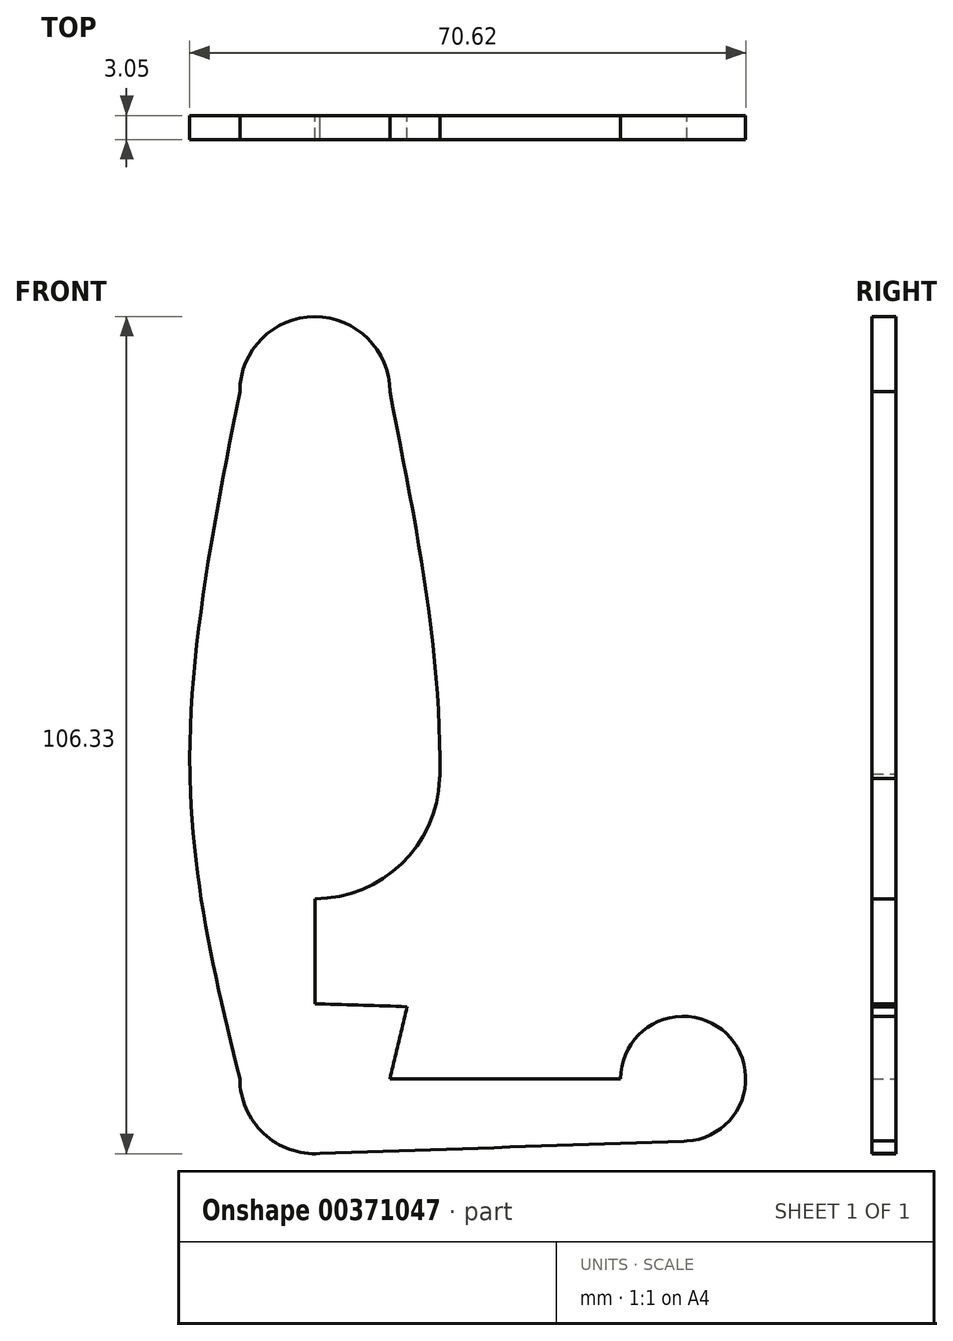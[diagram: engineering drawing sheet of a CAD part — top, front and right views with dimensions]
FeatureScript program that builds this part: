
annotation { "Feature Type Name" : "Feature", "Feature Type Description" : "" }
export const myFeature = defineFeature(function(context is Context, id is Id, definition is map)
    precondition{}
    {
        {
            var Q0;
            Q0=qCreatedBy(makeId("Front.planeOp"),FACE);
            var sketch = newSketch(context, id + "F0", { "sketchPlane" : qUnion([Q0])});
            skLineSegment(sketch, "E0", {"start": v(0, 0) * mm, "end": v(0, -38.73) * mm});
            skLineSegment(sketch, "E1", {"start": v(0, -38.73) * mm, "end": v(46.79, -38.73) * mm});
            skLineSegment(sketch, "E2", {"start": v(0, 0) * mm, "end": v(0, 48.56) * mm});
            skCircle(sketch, "E3", {"center": v(0, 48.56) * mm, "radius": 9.53 * mm});
            skCircle(sketch, "E4", {"center": v(0, 0) * mm, "radius": 15.88 * mm});
            skCircle(sketch, "E5", {"center": v(0, -38.73) * mm, "radius": 9.53 * mm});
            skCircle(sketch, "E6", {"center": v(46.79, -38.73) * mm, "radius": 7.94 * mm});
            skFitSpline(sketch, "E7", {"points": [v(-9.53, 48.56) * mm, v(-15.88, 0) * mm, v(-9.52, -38.73) * mm], "startDerivative": vector(-18.76, -94.67) * mm, "endDerivative": vector(19.46, -79.62) * mm});
            skFitSpline(sketch, "E8", {"points": [v(9.53, 48.56) * mm, v(15.88, 0) * mm, v(9.52, -38.73) * mm], "startDerivative": vector(18.76, -94.67) * mm, "endDerivative": vector(-19.46, -79.62) * mm});
            skFitSpline(sketch, "E9", {"points": [v(0, -29.2) * mm, v(46.68, -30.8) * mm, v(46.49, -30.8) * mm], "startDerivative": vector(74.56, -2.34) * mm, "endDerivative": vector(-4.82, -0.25) * mm});
            skFitSpline(sketch, "E10", {"points": [v(0, -48.25) * mm, v(47.24, -46.65) * mm], "startDerivative": vector(47.25, 1.59) * mm, "endDerivative": vector(47.25, 1.59) * mm});
            skSolve(sketch);
        }
        {
            var Q0;
            {var subQ0=sQuery(id+"F0.wireOp",EDGE,"E8");var subQ1=sQuery(id+"F0.wireOp",EDGE,"E4");var subQ2=makeQuery(id+"F0.imprint","INTERSECT",VERTEX,{"disambiguationData":[OD(1.0)],"derivedFrom":[subQ1,subQ0]});Q0=makeQuery(id+"F0.imprint","IMPRINT",FACE,{"disambiguationData":[TD([[makeQuery(id+"F0.imprint","IMPRINT",EDGE,{"disambiguationData":[TD([[subQ2,1.0]])],"derivedFrom":subQ1}),-1.0]])]});}
            var Q1;
            {var subQ1=sQuery(id+"F0.wireOp",EDGE,"E6");var subQ8=makeQuery(id+"F0.imprint","IMPRINT",VERTEX,{"derivedFrom":subQ1});Q1=makeQuery(id+"F0.imprint","IMPRINT",FACE,{"disambiguationData":[TD([[makeQuery(id+"F0.imprint","IMPRINT",EDGE,{"disambiguationData":[TD([[subQ8,1.0]])],"derivedFrom":subQ1}),1.0]])]});}
            var Q2;
            {var subQ3=sQuery(id+"F0.wireOp",EDGE,"E0");var subQ6=sQuery(id+"F0.wireOp",EDGE,"E2");var subQ8=makeQuery(id+"F0.imprint","INTERSECT",VERTEX,{"derivedFrom":[subQ3,subQ6]});Q2=makeQuery(id+"F0.imprint","IMPRINT",FACE,{"disambiguationData":[TD([[makeQuery(id+"F0.imprint","IMPRINT",EDGE,{"disambiguationData":[TD([[subQ8,-1.0]])],"derivedFrom":subQ3}),1.0]])]});}
            var Q3;
            {var subQ1=sQuery(id+"F0.wireOp",EDGE,"E6");var subQ3=makeQuery(id+"F0.imprint","IMPRINT",VERTEX,{"derivedFrom":subQ1});Q3=makeQuery(id+"F0.imprint","IMPRINT",FACE,{"disambiguationData":[TD([[makeQuery(id+"F0.imprint","IMPRINT",EDGE,{"disambiguationData":[TD([[subQ3,1.0]])],"derivedFrom":subQ1}),-1.0]])]});}
            var Q4;
            {var subQ3=sQuery(id+"F0.wireOp",EDGE,"E0");var subQ6=sQuery(id+"F0.wireOp",EDGE,"E2");var subQ8=makeQuery(id+"F0.imprint","INTERSECT",VERTEX,{"derivedFrom":[subQ3,subQ6]});Q4=makeQuery(id+"F0.imprint","IMPRINT",FACE,{"disambiguationData":[TD([[makeQuery(id+"F0.imprint","IMPRINT",EDGE,{"disambiguationData":[TD([[subQ8,-1.0]])],"derivedFrom":subQ3}),-1.0]])]});}
            var Q5;
            {var subQ0=sQuery(id+"F0.wireOp",EDGE,"E5");var subQ1=makeQuery(id+"F0.imprint","INTERSECT",VERTEX,{"derivedFrom":[subQ0,sQuery(id+"F0.wireOp",EDGE,"E7")]});Q5=makeQuery(id+"F0.imprint","IMPRINT",FACE,{"disambiguationData":[TD([[makeQuery(id+"F0.imprint","IMPRINT",EDGE,{"disambiguationData":[TD([[subQ1,-1.0]])],"derivedFrom":subQ0}),1.0]])]});}
            var Q6;
            {var subQ0=sQuery(id+"F0.wireOp",EDGE,"E3");var subQ1=makeQuery(id+"F0.imprint","INTERSECT",VERTEX,{"derivedFrom":[subQ0,sQuery(id+"F0.wireOp",EDGE,"E7")]});Q6=makeQuery(id+"F0.imprint","IMPRINT",FACE,{"disambiguationData":[TD([[makeQuery(id+"F0.imprint","IMPRINT",EDGE,{"disambiguationData":[TD([[subQ1,1.0]])],"derivedFrom":subQ0}),1.0]])]});}
            var Q7;
            {var subQ3=sQuery(id+"F0.wireOp",EDGE,"E4");var subQ5=sQuery(id+"F0.wireOp",EDGE,"E7");var subQ6=makeQuery(id+"F0.imprint","INTERSECT",VERTEX,{"disambiguationData":[OD(1.0)],"derivedFrom":[subQ3,subQ5]});Q7=makeQuery(id+"F0.imprint","IMPRINT",FACE,{"disambiguationData":[TD([[makeQuery(id+"F0.imprint","IMPRINT",EDGE,{"disambiguationData":[TD([[subQ6,-1.0]])],"derivedFrom":subQ3}),-1.0]])]});}
            var Q8;
            {var subQ0=sQuery(id+"F0.wireOp",EDGE,"E1");var subQ1=sQuery(id+"F0.wireOp",EDGE,"E0");var subQ2=makeQuery(id+"F0.imprint","INTERSECT",VERTEX,{"derivedFrom":[subQ1,subQ0]});Q8=makeQuery(id+"F0.imprint","IMPRINT",FACE,{"disambiguationData":[TD([[makeQuery(id+"F0.imprint","IMPRINT",EDGE,{"disambiguationData":[TD([[subQ2,1.0]])],"derivedFrom":subQ1}),1.0]])]});}
            var Q9;
            {var subQ1=sQuery(id+"F0.wireOp",EDGE,"E1");var subQ3=sQuery(id+"F0.wireOp",EDGE,"E6");var subQ4=makeQuery(id+"F0.imprint","INTERSECT",VERTEX,{"derivedFrom":[subQ1,subQ3]});Q9=makeQuery(id+"F0.imprint","IMPRINT",FACE,{"disambiguationData":[TD([[makeQuery(id+"F0.imprint","IMPRINT",EDGE,{"disambiguationData":[TD([[subQ4,-1.0]])],"derivedFrom":subQ3}),-1.0]])]});}
            var Q10;
            {var subQ0=sQuery(id+"F0.wireOp",EDGE,"E3");var subQ1=sQuery(id+"F0.wireOp",EDGE,"E2");var subQ2=makeQuery(id+"F0.imprint","INTERSECT",VERTEX,{"derivedFrom":[subQ1,subQ0]});Q10=makeQuery(id+"F0.imprint","IMPRINT",FACE,{"disambiguationData":[TD([[makeQuery(id+"F0.imprint","IMPRINT",EDGE,{"disambiguationData":[TD([[subQ2,1.0]])],"derivedFrom":subQ1}),1.0]])]});}
            var Q11;
            {var subQ0=sQuery(id+"F0.wireOp",EDGE,"E3");var subQ1=sQuery(id+"F0.wireOp",EDGE,"E2");var subQ2=makeQuery(id+"F0.imprint","INTERSECT",VERTEX,{"derivedFrom":[subQ1,subQ0]});Q11=makeQuery(id+"F0.imprint","IMPRINT",FACE,{"disambiguationData":[TD([[makeQuery(id+"F0.imprint","IMPRINT",EDGE,{"disambiguationData":[TD([[subQ2,1.0]])],"derivedFrom":subQ1}),-1.0]])]});}
            var Q12;
            {var subQ0=sQuery(id+"F0.wireOp",EDGE,"E8");var subQ3=sQuery(id+"F0.wireOp",EDGE,"E9");var subQ5=makeQuery(id+"F0.imprint","INTERSECT",VERTEX,{"derivedFrom":[subQ0,subQ3]});Q12=makeQuery(id+"F0.imprint","IMPRINT",FACE,{"disambiguationData":[TD([[makeQuery(id+"F0.imprint","IMPRINT",EDGE,{"disambiguationData":[TD([[subQ5,1.0]])],"derivedFrom":subQ3}),-1.0]])]});}
            var Q13;
            {var subQ0=sQuery(id+"F0.wireOp",EDGE,"E7");var subQ1=sQuery(id+"F0.wireOp",EDGE,"E4");var subQ2=makeQuery(id+"F0.imprint","INTERSECT",VERTEX,{"disambiguationData":[OD(0.0)],"derivedFrom":[subQ1,subQ0]});Q13=makeQuery(id+"F0.imprint","IMPRINT",FACE,{"disambiguationData":[TD([[makeQuery(id+"F0.imprint","IMPRINT",EDGE,{"disambiguationData":[TD([[subQ2,-1.0]])],"derivedFrom":subQ1}),1.0]])]});}
            var Q14;
            {var subQ0=sQuery(id+"F0.wireOp",EDGE,"E8");var subQ1=sQuery(id+"F0.wireOp",EDGE,"E4");var subQ2=makeQuery(id+"F0.imprint","INTERSECT",VERTEX,{"disambiguationData":[OD(0.0)],"derivedFrom":[subQ1,subQ0]});Q14=makeQuery(id+"F0.imprint","IMPRINT",FACE,{"disambiguationData":[TD([[makeQuery(id+"F0.imprint","IMPRINT",EDGE,{"disambiguationData":[TD([[subQ2,1.0]])],"derivedFrom":subQ1}),1.0]])]});}
            var Q15;
            {var subQ0=sQuery(id+"F0.wireOp",EDGE,"E10");var subQ1=sQuery(id+"F0.wireOp",EDGE,"E5");var subQ2=makeQuery(id+"F0.imprint","INTERSECT",VERTEX,{"disambiguationData":[OD(0.0)],"derivedFrom":[subQ1,subQ0]});Q15=makeQuery(id+"F0.imprint","IMPRINT",FACE,{"disambiguationData":[TD([[makeQuery(id+"F0.imprint","IMPRINT",EDGE,{"disambiguationData":[TD([[subQ2,-1.0]])],"derivedFrom":subQ1}),1.0]])]});}
            var Q16;
            {var subQ0=sQuery(id+"F0.wireOp",EDGE,"E10");var subQ1=sQuery(id+"F0.wireOp",EDGE,"E6");var subQ2=makeQuery(id+"F0.imprint","INTERSECT",VERTEX,{"disambiguationData":[OD(0.0)],"derivedFrom":[subQ1,subQ0]});Q16=makeQuery(id+"F0.imprint","IMPRINT",FACE,{"disambiguationData":[TD([[makeQuery(id+"F0.imprint","IMPRINT",EDGE,{"disambiguationData":[TD([[subQ2,1.0]])],"derivedFrom":subQ1}),1.0]])]});}
            var Q17;
            {var subQ0=sQuery(id+"F0.wireOp",EDGE,"E9");var subQ1=sQuery(id+"F0.wireOp",EDGE,"E5");var subQ3=makeQuery(id+"F0.imprint","INTERSECT",VERTEX,{"derivedFrom":[subQ1,subQ0]});Q17=makeQuery(id+"F0.imprint","IMPRINT",FACE,{"disambiguationData":[TD([[makeQuery(id+"F0.imprint","IMPRINT",EDGE,{"disambiguationData":[TD([[subQ3,-1.0]])],"derivedFrom":subQ1}),1.0]])]});}
            var Q18;
            {var subQ0=sQuery(id+"F0.wireOp",EDGE,"E9");var subQ1=sQuery(id+"F0.wireOp",EDGE,"E6");var subQ2=makeQuery(id+"F0.imprint","INTERSECT",VERTEX,{"disambiguationData":[OD(0.0)],"derivedFrom":[subQ1,subQ0]});Q18=makeQuery(id+"F0.imprint","IMPRINT",FACE,{"disambiguationData":[TD([[makeQuery(id+"F0.imprint","IMPRINT",EDGE,{"disambiguationData":[TD([[subQ2,1.0]])],"derivedFrom":subQ1}),1.0]])]});}
            extrude(context, id + "F1", {"entities" : qUnion([Q0, Q1, Q2, Q3, Q4, Q5, Q6, Q7, Q8, Q9, Q10, Q11, Q12, Q13, Q14, Q15, Q16, Q17, Q18]), "depth" : 3.05 * mm});
        }
    });
